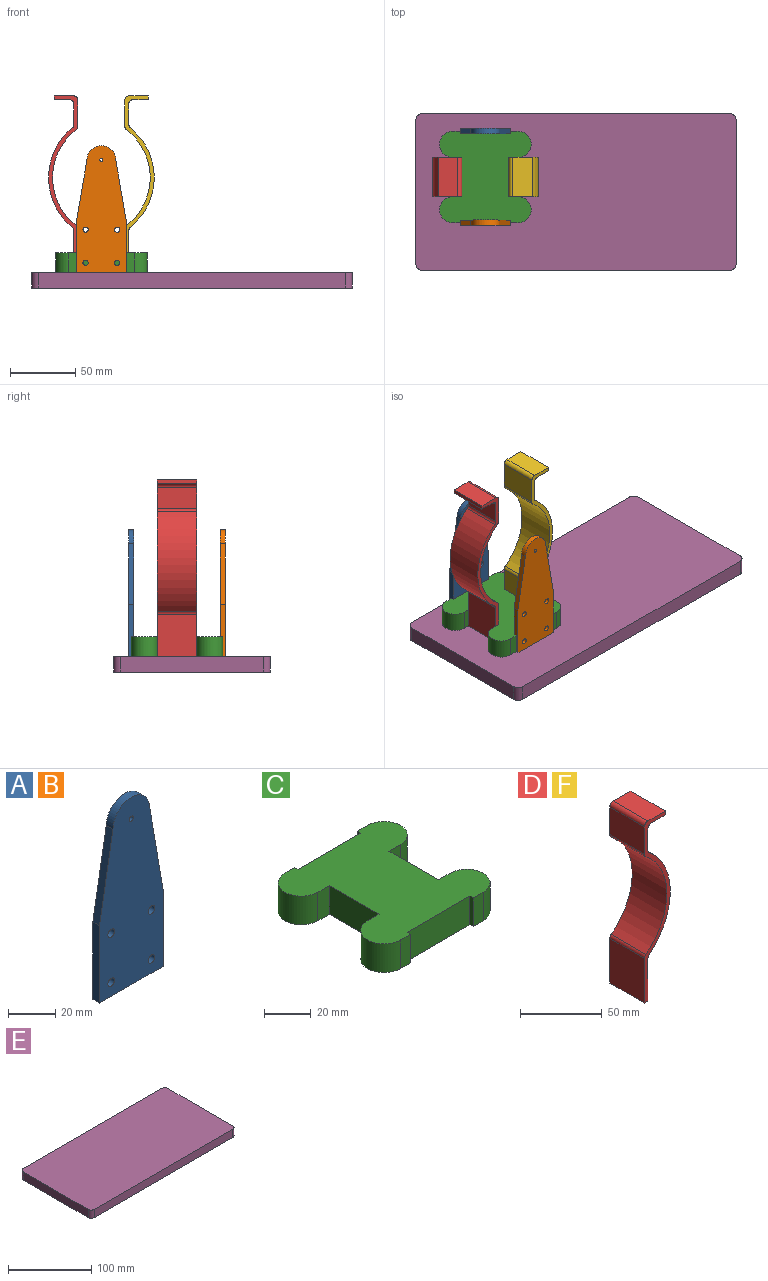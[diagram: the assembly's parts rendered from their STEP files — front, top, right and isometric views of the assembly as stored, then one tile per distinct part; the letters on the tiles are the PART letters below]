
ASSEMBLY  parts=6 mates=14
PART A: 13 faces, bbox 38x4x97 mm
  f0: plane 46x8mm, normal (-0.99,0,0.17), area 186.8mm2, adj f1,f9,f11,f12
  f1: plane 40x4mm, normal (-1,0,0), area 160mm2, adj f0,f2,f11,f12
  f2: plane 38x4mm, normal (0,0,-1), area 152mm2, adj f1,f3,f11,f12
  f3: plane 40x4mm, normal (1,0,0), area 160mm2, adj f2,f4,f11,f12
  f4: plane 46x8mm, normal (0.99,0,0.17), area 186.8mm2, adj f3,f9,f11,f12
  f5: cylinder r=2mm len=4mm, axis (0,1,0), area 50.3mm2, adj f11,f12
  f6: cylinder r=2mm len=4mm, axis (0,1,0), area 50.3mm2, adj f11,f12
  f7: cylinder r=2mm len=4mm, axis (0,1,0), area 50.3mm2, adj f11,f12
  f8: cylinder r=1.25mm len=4mm, axis (0,1,0), area 31.4mm2, adj f11,f12
  f9: cylinder r=11mm len=22mm, axis (0,1,0), area 138.2mm2, adj f0,f4,f11,f12
  f10: cylinder r=2mm len=4mm, axis (0,1,0), area 50.3mm2, adj f11,f12
  f11: plane 97x38mm, normal (0,-1,0), area 3034.9mm2, adj f0,f1,f2,f3,f4,f5,f6,f7
  f12: plane 97x38mm, normal (0,1,0), area 3034.9mm2, adj f0,f1,f2,f3,f4,f5,f6,f7
PART B: same geometry as A
PART C: 22 faces, bbox 70x70x15 mm
  f0: plane 15x2mm, normal (1,0,0), area 30mm2, adj f1,f19,f20,f21
  f1: plane 38x15mm, normal (0,-1,0), area 570mm2, adj f0,f2,f20,f21
  f2: plane 15x2mm, normal (-1,0,0), area 30mm2, adj f1,f3,f20,f21
  f3: plane 15x6mm, normal (0,-1,0), area 90mm2, adj f2,f4,f20,f21
  f4: cylinder r=10mm len=20mm, axis (0,0,-1), area 471.2mm2, adj f3,f5,f20,f21
  f5: plane 15x7mm, normal (0,1,0), area 105mm2, adj f4,f6,f20,f21
  f6: plane 30x15mm, normal (1,0,0), area 450mm2, adj f5,f7,f20,f21
  f7: plane 15x7mm, normal (0,-1,0), area 105mm2, adj f6,f8,f20,f21
  f8: cylinder r=10mm len=20mm, axis (0,0,-1), area 471.2mm2, adj f7,f9,f20,f21
  f9: plane 15x6mm, normal (0,1,0), area 90mm2, adj f8,f10,f20,f21
  f10: plane 15x2mm, normal (-1,0,0), area 30mm2, adj f9,f11,f20,f21
  f11: plane 38x15mm, normal (0,1,0), area 570mm2, adj f10,f12,f20,f21
  f12: plane 15x2mm, normal (1,0,0), area 30mm2, adj f11,f13,f20,f21
  f13: plane 15x6mm, normal (0,1,0), area 90mm2, adj f12,f14,f20,f21
  f14: cylinder r=10mm len=20mm, axis (0,0,-1), area 471.2mm2, adj f13,f15,f20,f21
  f15: plane 15x7mm, normal (0,-1,0), area 105mm2, adj f14,f16,f20,f21
  f16: plane 30x15mm, normal (-1,0,0), area 450mm2, adj f15,f17,f20,f21
  f17: plane 15x7mm, normal (0,1,0), area 105mm2, adj f16,f18,f20,f21
  f18: cylinder r=10mm len=20mm, axis (0,0,-1), area 471.2mm2, adj f17,f19,f20,f21
  f19: plane 15x6mm, normal (0,-1,0), area 90mm2, adj f0,f18,f20,f21
  f20: plane 70x70mm, normal (0,0,1), area 3556.3mm2, adj f0,f1,f2,f3,f4,f5,f6,f7
  f21: plane 70x70mm, normal (0,0,-1), area 3556.3mm2, adj f0,f1,f2,f3,f4,f5,f6,f7
PART D: 18 faces, bbox 22.4x30x135 mm
  f0: plane 30x15mm, normal (0,0,1), area 450mm2, adj f1,f15,f16,f17
  f1: cylinder r=3mm len=30mm, axis (0,1,0), area 141.4mm2, adj f0,f2,f16,f17
  f2: plane 30x20.48mm, normal (-1,0,0), area 614.5mm2, adj f1,f3,f16,f17
  f3: cylinder r=3mm len=30mm, axis (0,1,0), area 82.9mm2, adj f2,f4,f16,f17
  f4: cylinder r=46mm len=73.26mm, axis (0,1,0), area 2542.3mm2, adj f3,f5,f16,f17
  f5: cylinder r=3mm len=30mm, axis (0,1,0), area 82.9mm2, adj f4,f6,f16,f17
  f6: plane 33.48x30mm, normal (-1,0,0), area 1004.5mm2, adj f5,f7,f16,f17
  f7: plane 30x3mm, normal (0,0,-1), area 90mm2, adj f6,f8,f16,f17
  f8: plane 32.02x30mm, normal (1,0,0), area 960.6mm2, adj f7,f9,f16,f17
  f9: cylinder r=3mm len=30mm, axis (0,1,0), area 80.3mm2, adj f8,f10,f16,f17
  f10: cylinder r=49mm len=76.29mm, axis (0,1,0), area 2623mm2, adj f9,f11,f16,f17
  f11: cylinder r=3mm len=30mm, axis (0,1,0), area 80.3mm2, adj f10,f12,f16,f17
  f12: plane 30x16.02mm, normal (1,0,0), area 480.6mm2, adj f11,f13,f16,f17
  f13: cylinder r=3mm len=30mm, axis (0,1,0), area 141.4mm2, adj f12,f14,f16,f17
  f14: plane 30x12mm, normal (0,0,-1), area 360mm2, adj f13,f15,f16,f17
  f15: plane 30x3mm, normal (1,0,0), area 90mm2, adj f0,f14,f16,f17
  f16: plane 135x22.36mm, normal (0,-1,0), area 487.3mm2, adj f0,f1,f2,f3,f4,f5,f6,f7
  f17: plane 135x22.36mm, normal (0,1,0), area 487.3mm2, adj f0,f1,f2,f3,f4,f5,f6,f7
PART E: 10 faces, bbox 245x120x12 mm
  f0: plane 110x12mm, normal (1,0,0), area 1320mm2, adj f4,f5,f6,f9
  f1: plane 235x12mm, normal (0,1,0), area 2820mm2, adj f4,f5,f6,f7
  f2: plane 110x12mm, normal (-1,0,0), area 1320mm2, adj f4,f5,f7,f8
  f3: plane 235x12mm, normal (0,-1,0), area 2820mm2, adj f4,f5,f8,f9
  f4: plane 245x120mm, normal (0,0,1), area 29378.5mm2, adj f0,f1,f2,f3,f6,f7,f8,f9
  f5: plane 245x120mm, normal (0,0,-1), area 29378.5mm2, adj f0,f1,f2,f3,f6,f7,f8,f9
  f6: cylinder r=5mm len=12mm, axis (0,0,1), area 94.2mm2, adj f0,f1,f4,f5
  f7: cylinder r=5mm len=12mm, axis (0,0,-1), area 94.2mm2, adj f1,f2,f4,f5
  f8: cylinder r=5mm len=12mm, axis (0,0,1), area 94.2mm2, adj f2,f3,f4,f5
  f9: cylinder r=5mm len=12mm, axis (0,0,-1), area 94.2mm2, adj f0,f3,f4,f5
PART F: same geometry as D
PLACE A rot(axis=(0,0,-1),180deg) t=(-233.95,154.47,-23.57)mm
PLACE B rot(axis=(0,0,-1),180deg) t=(-233.95,84.47,-23.57)mm
PLACE C rot(axis=(0,0,-1),180deg) t=(-233.95,121.47,-43.57)mm
PLACE D rot(axis=(0,0,-1),180deg) t=(-251.95,106.47,-43.57)mm
PLACE E t=(-164.63,110.06,-55.57)mm
PLACE F t=(-215.95,136.47,-43.57)mm
MATE planar A.f12 <-> C.f1  axis (0,-1,0) through (-233.95,154.47,-0.63)mm
MATE planar B.f11 <-> C.f11  axis (0,1,0) through (-233.95,88.47,-0.63)mm
MATE planar D.f6 <-> C.f6  axis (1,0,0) through (-251.95,121.47,-26.83)mm
MATE planar B.f3 <-> C.f10  axis (-1,0,0) through (-252.95,86.47,-23.57)mm
MATE planar F.f6 <-> C.f16  axis (-1,0,0) through (-215.95,121.47,-43.57)mm
MATE planar A.f1 <-> C.f0  axis (1,0,0) through (-214.95,156.47,-23.57)mm
MATE planar C.f21 <-> E.f4  axis (0,0,-1) through (-233.95,121.47,-43.57)mm
MATE planar B.f2 <-> E.f4  axis (0,0,-1) through (-233.95,86.47,-43.57)mm
MATE planar E.f4 <-> C.f21  axis (0,0,1) through (-164.63,110.06,-43.57)mm
MATE planar D.f7 <-> E.f4  axis (0,0,-1) through (-253.45,121.47,-43.57)mm
MATE planar F.f7 <-> E.f4  axis (0,0,-1) through (-214.45,121.47,-43.57)mm
MATE planar D.f16 <-> C.f5  axis (0,1,0) through (-251.95,136.47,-26.83)mm
MATE planar F.f16 <-> C.f15  axis (0,-1,0) through (-214.45,106.47,-43.57)mm
MATE planar A.f2 <-> E.f4  axis (0,0,-1) through (-233.95,156.47,-43.57)mm
